# Revit family: IS_Ceraplus_B8221_BIM_DE
name_source: partatom
category: Plumbing Fixtures
revit_build: Autodesk Revit MEP 2015 (Build: 20140606_1530(x64)
units: mm (PartAtom-declared; Revit-internal decimal feet)

## types (1)
- B8221AA - IS WT-Sicherheitsarm.CERAPLUS,o.Ablgarn, Bedienhebel 180mm, Ausld. 108mm, Chrom
    Assembly Code = C1030211
    BIMobject category = Basins
    BOSUseNativeGeometries = 1
    Brand url = http://www.idealstandard.co.uk
    Description = B8221AA CERAPLUS anti vandal single lever one hole basin mixer, no pop-up waste
    EAN code = https://3800861002864
    Edition number = 1
    FaucetFunction = mixed
    FaucetOperation = leverhandle
    FaucetType = pillar
    FlushRate = 0 m³
    FlushingRate = 0
    IFC Classification = Valve
    IfcExportAs = IfcValveType
    IfcExportType = BRASSWARE BASIN
    Installation instructions = http://www.idealspec.co.uk
    Manufacturer name = Ideal Standard
    ManufacturerURL = www.idealstandard.com
    Material = Brass
    Material main = Brassware
    Model = B8221AA
    ModelNumber = B8221AA
    NBS Reference Code = 75-70-52-96
    NBS Reference Description = Water Supply Systems Control Systems
    Name = CERAPLUS anti vandal single lever one hole basin mixer, no pop-up waste
    NettWeight = 1,665 kg
    Nominal height = 144
    Nominal width = 164
    NominalDepth = 0 mm  [stored 0 ft]
    NominalHeight = 144 mm  [stored 0.472441 ft]
    NominalLength = 0 mm  [stored 0 ft]
    NominalWidth = 164 mm  [stored 0.538058 ft]
    OmniClass Code = 23.45.55.18
    OmniClass Description = Mixing Faucets
    Product Guid = aca75aa0-11f3-4e63-a6e0-c2e9aaf6203f
    Product SKU = B8221
    Product data url = https://bimobject.com
    Product family = Sanitary
    Product group = Washbasin taps
    Product name = Ceraplus Basin Mixer Rim
    Product url = www.idealstandard.de/produkte
    ProductInformation = www.idealstandard.de/produkte
    QR code = http://bimobject.com
    Shape = Sculptured
    Space = Internal
    SpareParts = www.idealstandard.de/ersatzteile
    Technical description = www.idealstandard.de/produkte
    URL = www.idealstandard.com
    Uniclass 2.0 Code = SS-75-70-52-96
    Uniclass 2.0 Description = Water Supply Systems Control Systems
    Uniclass 2015 Code = Pr_40_20_87_96
    Uniclass 2015 Name = Washbasin manual water supply sets
    ValveMechanism = ceramic disc
    ValveOperation = lever
    Version = 1
    VolumeUnits = Litres
    WarrantyDurationParts = 5
    WarrantyDurationUnit = year
    Weight Net (Kg) = 1.665
    WorkingPressure = 1-5 Bar

note: [stored X ft] marks values corroborated as IEEE doubles in the binary element streams (Revit-internal decimal feet)

## geometry (parser evidence)
native form markers: Blend x4, Sweep x1
no freeform markers — native parametric forms only
